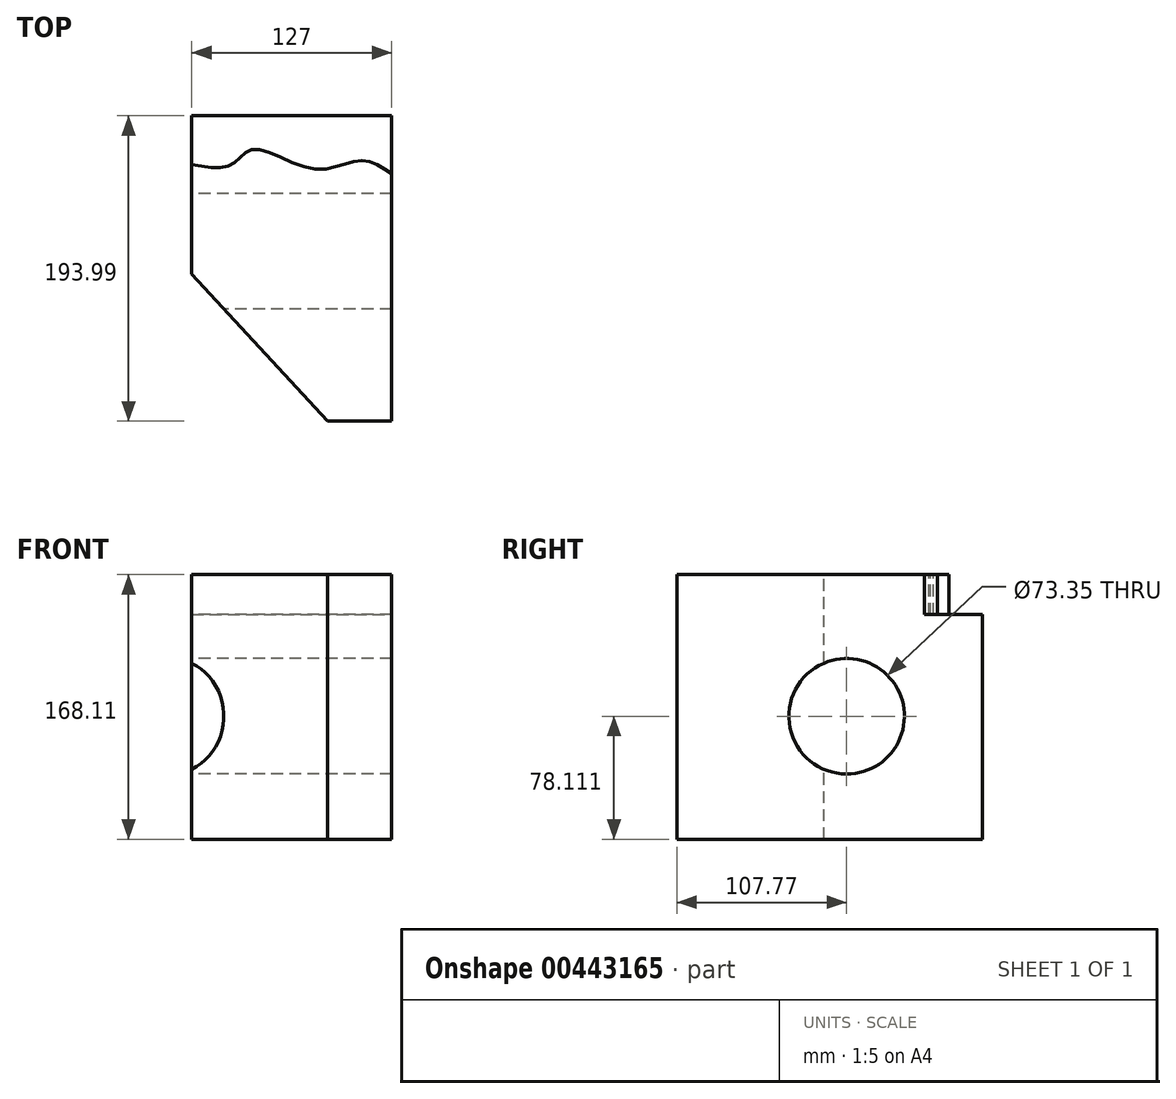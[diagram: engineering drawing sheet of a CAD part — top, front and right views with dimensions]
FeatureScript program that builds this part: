
annotation { "Feature Type Name" : "Feature", "Feature Type Description" : "" }
export const myFeature = defineFeature(function(context is Context, id is Id, definition is map)
    precondition{}
    {
        {
            var Q0;
            Q0=qCreatedBy(makeId("Right.planeOp"),FACE);
            var sketch = newSketch(context, id + "F0", { "sketchPlane" : qUnion([Q0])});
            skLineSegment(sketch, "E0.bottom", {"start": v(-107.77, 108.1) * mm, "end": v(86.22, 108.1) * mm});
            skLineSegment(sketch, "E0.top", {"start": v(-107.77, -60) * mm, "end": v(86.22, -60) * mm});
            skLineSegment(sketch, "E0.left", {"start": v(-107.77, 108.1) * mm, "end": v(-107.77, -60) * mm});
            skLineSegment(sketch, "E0.right", {"start": v(86.22, 108.1) * mm, "end": v(86.22, -60) * mm});
            skCircle(sketch, "E1", {"center": v(0, 18.11) * mm, "radius": 36.68 * mm});
            skSolve(sketch);
        }
        {
            var Q0;
            Q0=makeQuery(id+"F0.imprint","IMPRINT",FACE,{"disambiguationData":[TD([[makeQuery(id+"F0.imprint","IMPRINT",EDGE,{"derivedFrom":sQuery(id+"F0.wireOp",EDGE,"E0.bottom")}),-1.0]])]});
            extrude(context, id + "F1", {"entities" : qUnion([Q0]), "depth" : 127 * mm});
        }
        {
            var Q0;
            Q0=makeQuery(id+"F1.opExtrude","SWEPT_FACE",FACE,{"disambiguationData":[OSD([sQuery(id+"F0.wireOp",EDGE,"E0.bottom")])]});
            var sketch = newSketch(context, id + "F2", { "sketchPlane" : qUnion([Q0])});
            skFitSpline(sketch, "E2", {"points": [v(0, 55.22) * mm, v(25.4, 55.22) * mm, v(38.9, 64.92) * mm, v(78.11, 52.27) * mm, v(107.21, 57.75) * mm, v(127, 49.32) * mm], "startDerivative": vector(146.6, -26.29) * mm, "endDerivative": vector(105.28, -71.66) * mm});
            skSolve(sketch);
        }
        {
            var Q0;
            Q0 = qSketchRegion(id + "F2", true);
            var Q1;
            {var subQ0=sQuery(id+"F2.wireOp",EDGE,"E2");Q1=makeQuery(id+"F2.imprint","IMPRINT",FACE,{"disambiguationData":[TD([[makeQuery(id+"F2.imprint","IMPRINT",EDGE,{"derivedFrom":subQ0}),1.0]])]});}
            extrude(context, id + "F3", {"entities" : qUnion([Q0, Q1]), "operationType" : NewBodyOperationType.REMOVE, "oppositeDirection" : true, "depth" : 25.4 * mm});
        }
        {
            var Q0;
            Q0=makeQuery(id+"F1.opExtrude","SWEPT_FACE",FACE,{"disambiguationData":[OSD([sQuery(id+"F0.wireOp",EDGE,"E0.bottom")])]});
            var sketch = newSketch(context, id + "F4", { "sketchPlane" : qUnion([Q0])});
            skLineSegment(sketch, "E3", {"start": v(0, -14.52) * mm, "end": v(86.21, -107.77) * mm});
            skSolve(sketch);
        }
        {
            var Q0;
            Q0 = qSketchRegion(id + "F4", true);
            var Q1;
            {var subQ0=sQuery(id+"F4.wireOp",EDGE,"E3");Q1=makeQuery(id+"F4.imprint","IMPRINT",FACE,{"disambiguationData":[TD([[makeQuery(id+"F4.imprint","IMPRINT",EDGE,{"derivedFrom":subQ0}),-1.0]])]});}
            extrude(context, id + "F5", {"entities" : qUnion([Q0, Q1]), "operationType" : NewBodyOperationType.REMOVE, "endBound" : BoundingType.UP_TO_NEXT, "oppositeDirection" : true, "depth" : 25.4 * mm});
        }
    });
